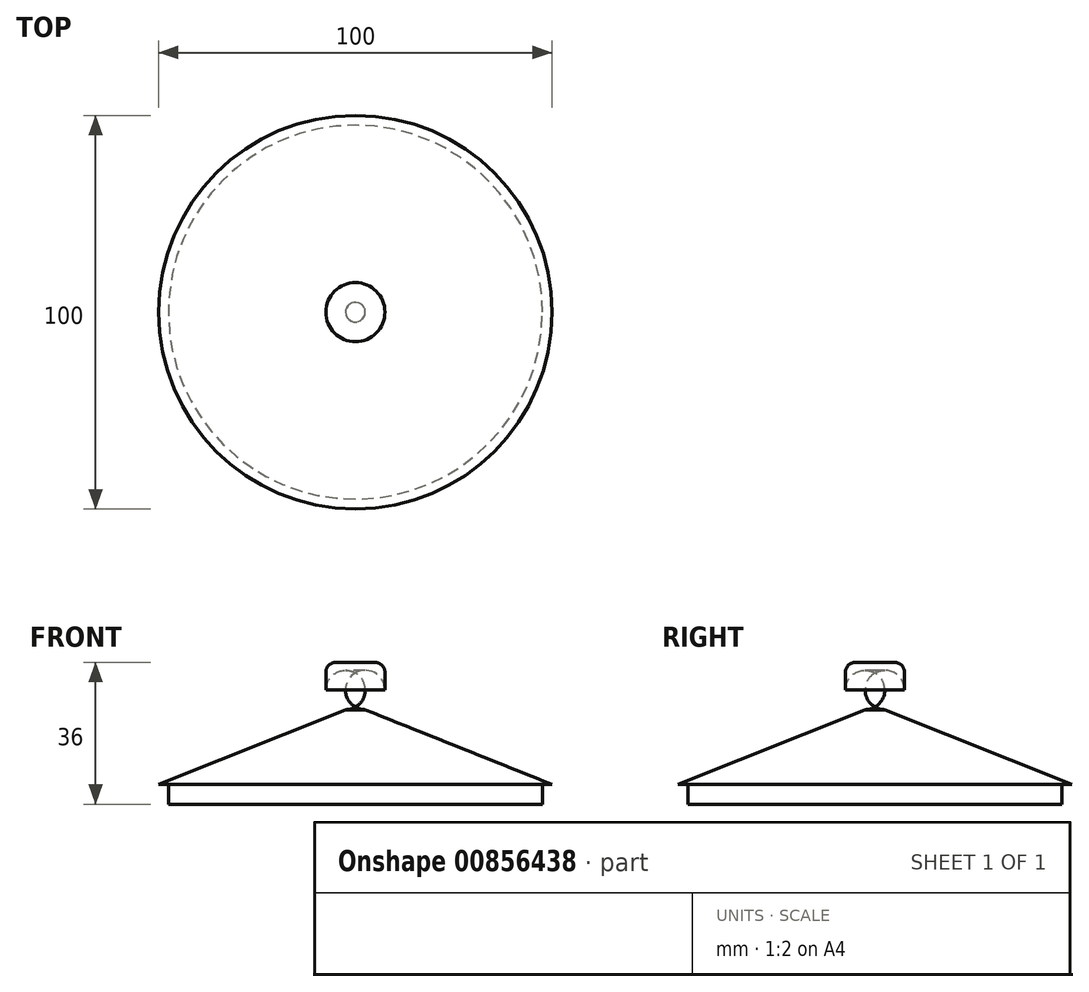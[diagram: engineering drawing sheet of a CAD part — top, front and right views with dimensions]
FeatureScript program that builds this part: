
annotation { "Feature Type Name" : "Feature", "Feature Type Description" : "" }
export const myFeature = defineFeature(function(context is Context, id is Id, definition is map)
    precondition{}
    {
        {
            var Q0;
            Q0=qCreatedBy(makeId("Top.planeOp"),FACE);
            var sketch = newSketch(context, id + "F0", { "sketchPlane" : qUnion([Q0])});
            skCircle(sketch, "E0", {"center": v(0, 0) * mm, "radius": 50 * mm});
            skSolve(sketch);
        }
        {
            var Q0;
            Q0=qCreatedBy(makeId("Top.planeOp"),FACE);
            cPlane(context, id + "F1", {"entities" : qUnion([Q0]), "cplaneType" : CPlaneType.OFFSET, "offset" : 19 * mm, "width" : 150 * mm, "height" : 150 * mm});
        }
        {
            var Q0;
            Q0=qCreatedBy(id+"F1.planeOp",FACE);
            var sketch = newSketch(context, id + "F2", { "sketchPlane" : qUnion([Q0])});
            skCircle(sketch, "E1", {"center": v(0, 0) * mm, "radius": 2.5 * mm});
            skSolve(sketch);
        }
        {
            var Q0;
            Q0=qSketchRegion(id+"F2",true);
            var Q1;
            Q1=qSketchRegion(id+"F0",true);
            loft(context, id + "F3", {"sheetProfilesArray" : [{ "sheetProfileEntities" : qUnion([Q0]) }, { "sheetProfileEntities" : qUnion([Q1]) }]});
        }
        {
            var Q0;
            Q0=makeQuery(id+"F2.imprint","IMPRINT",FACE,{"disambiguationData":[TD([[makeQuery(id+"F2.imprint","IMPRINT",EDGE,{"derivedFrom":sQuery(id+"F2.wireOp",EDGE,"E1")}),1.0]])]});
            var Q1;
            Q1=makeQuery(id+"F0.imprint","IMPRINT",FACE,{"disambiguationData":[TD([[makeQuery(id+"F0.imprint","IMPRINT",EDGE,{"derivedFrom":sQuery(id+"F0.wireOp",EDGE,"E0")}),1.0]])]});
            loft(context, id + "F4", {"sheetProfilesArray" : [{ "sheetProfileEntities" : qUnion([Q0]) }, { "sheetProfileEntities" : qUnion([Q1]) }]});
        }
        {
            var Q0;
            Q0=qCreatedBy(id+"F1.planeOp",FACE);
            var sketch = newSketch(context, id + "F5", { "sketchPlane" : qUnion([Q0])});
            skCircle(sketch, "E2", {"center": v(0, 0) * mm, "radius": 7.5 * mm});
            skSolve(sketch);
        }
        {
            var Q0;
            Q0=makeQuery(id+"F5.imprint","IMPRINT",FACE,{"disambiguationData":[TD([[makeQuery(id+"F5.imprint","IMPRINT",EDGE,{"derivedFrom":sQuery(id+"F5.wireOp",EDGE,"E2")}),1.0]])]});
            extrude(context, id + "F6", {"entities" : qUnion([Q0]), "operationType" : NewBodyOperationType.ADD, "depth" : 12 * mm, "offsetDistance" : 25 * mm});
        }
        {
            var Q0;
            Q0=makeQuery(id+"F6.opExtrude","CAP_EDGE",EDGE,{"disambiguationData":[OSD([sQuery(id+"F5.wireOp",EDGE,"E2")])],"isStart":false});
            fillet(context, id + "F7", {"entities" : qUnion([Q0]), "radius" : 2.5 * mm, "tangentPropagation" : true, "allowEdgeOverflow" : false});
        }
        {
            var Q0;
            Q0=makeQuery(id+"F6.opExtrude","CAP_EDGE",EDGE,{"disambiguationData":[OSD([sQuery(id+"F5.wireOp",EDGE,"E2")])],"isStart":true});
            fillet(context, id + "F8", {"entities" : qUnion([Q0]), "radius" : 5 * mm, "tangentPropagation" : true, "allowEdgeOverflow" : false});
        }
        {
            var Q0;
            Q0=qCreatedBy(makeId("Top.planeOp"),FACE);
            var sketch = newSketch(context, id + "F9", { "sketchPlane" : qUnion([Q0])});
            skCircle(sketch, "E3", {"center": v(0, 0) * mm, "radius": 47.5 * mm});
            skSolve(sketch);
        }
        {
            var Q0;
            Q0=makeQuery(id+"F9.imprint","IMPRINT",FACE,{"disambiguationData":[TD([[makeQuery(id+"F9.imprint","IMPRINT",EDGE,{"derivedFrom":sQuery(id+"F9.wireOp",EDGE,"E3")}),1.0]])]});
            extrude(context, id + "F10", {"entities" : qUnion([Q0]), "operationType" : NewBodyOperationType.ADD, "oppositeDirection" : true, "depth" : 5 * mm, "offsetDistance" : 25 * mm});
        }
    });
